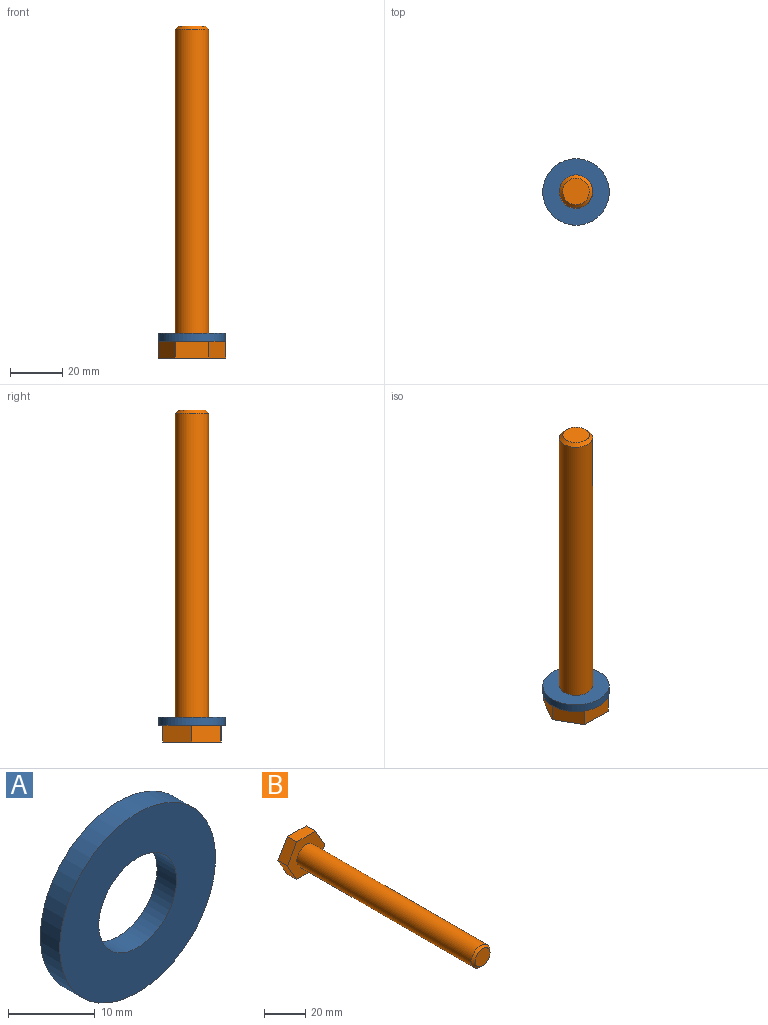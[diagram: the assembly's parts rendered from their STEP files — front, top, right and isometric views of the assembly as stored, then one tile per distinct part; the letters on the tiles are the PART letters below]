
ASSEMBLY  parts=2 mates=1
PART A: 4 faces, bbox 25.4x3.2x25.4 mm
  f0: cylinder r=6.35mm len=12.7mm, axis (0,1,0), area 126.7mm2, adj f2,f3
  f1: cylinder r=12.7mm len=25.4mm, axis (0,1,0), area 253.4mm2, adj f2,f3
  f2: plane 25.4x25.4mm, normal (0,-1,0), area 380mm2, adj f0,f1
  f3: plane 25.4x25.4mm, normal (0,1,0), area 380mm2, adj f0,f1
PART B: 11 faces, bbox 25.7x127x22.3 mm
  f0: plane 11.15x6.35mm, normal (0.87,0,0.5), area 81.5mm2, adj f1,f5,f6,f7
  f1: plane 12.83x6.35mm, normal (0.01,0,1), area 81.5mm2, adj f0,f2,f6,f7
  f2: plane 11.08x6.48mm, normal (-0.86,0,0.5), area 81.5mm2, adj f1,f3,f6,f7
  f3: plane 11.15x6.35mm, normal (-0.87,0,-0.5), area 81.5mm2, adj f2,f4,f6,f7
  f4: plane 12.83x6.35mm, normal (-0.01,0,-1), area 81.5mm2, adj f3,f5,f6,f7
  f5: plane 11.08x6.48mm, normal (0.86,0,-0.5), area 81.5mm2, adj f0,f4,f6,f7
  f6: plane 25.66x22.3mm, normal (0,-1,0), area 301.1mm2, adj f0,f1,f2,f3,f4,f5,f8
  f7: plane 25.66x22.3mm, normal (0,1,0), area 427.8mm2, adj f0,f1,f2,f3,f4,f5
  f8: cylinder r=6.35mm len=119.38mm, axis (0,1,0), area 4763.1mm2, adj f6,f10
  f9: plane 10.16x10.16mm, normal (0,-1,0), area 81.1mm2, adj f10
  f10: cone r=5.08mm half-angle=45deg, axis (0,1,0), area 64.5mm2, adj f8,f9
PLACE A rot(axis=(1,0,0),90deg) t=(0,0,3.18)mm
PLACE B rot(axis=(-1,0,0),90deg) t=(0,0,-6.35)mm
MATE fastened A.f0 <-> B.f8  axis (0,0,-1) through (0,0,0)mm
